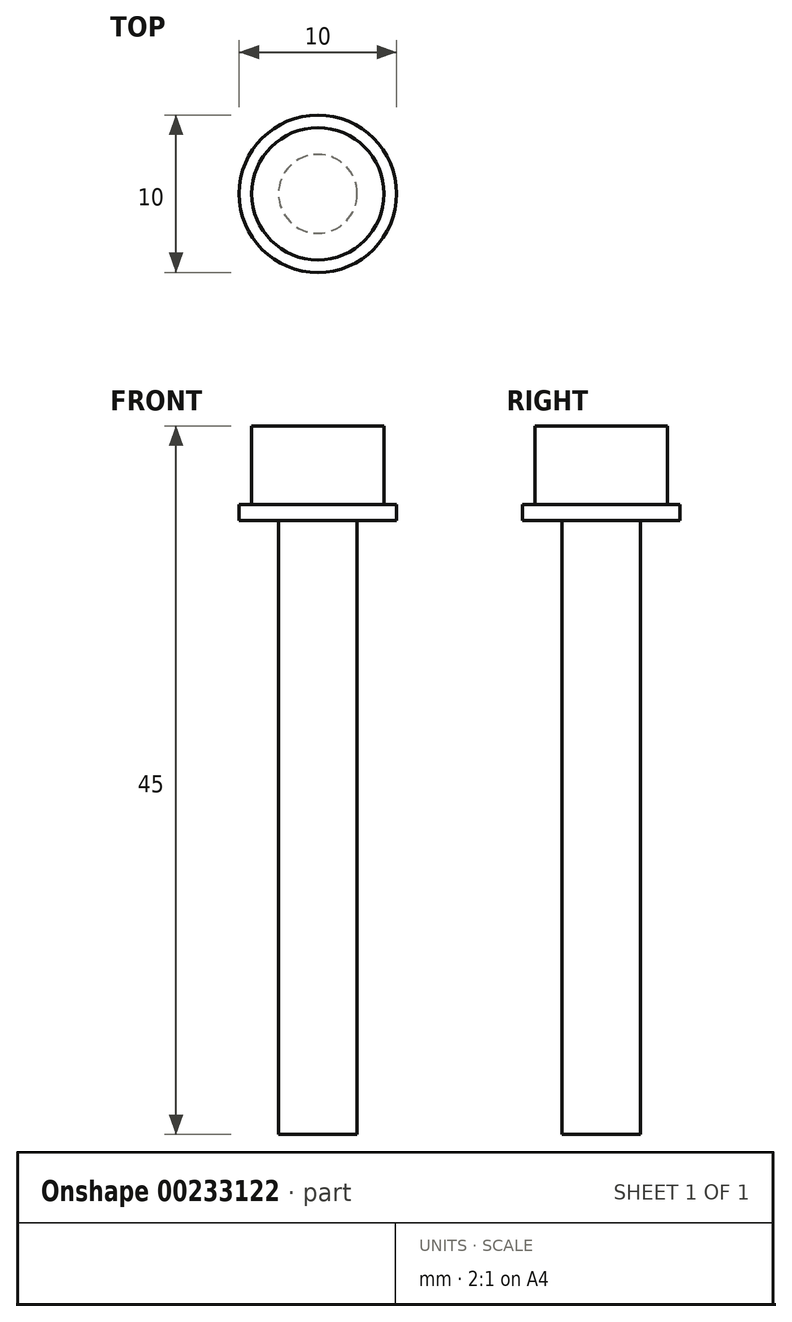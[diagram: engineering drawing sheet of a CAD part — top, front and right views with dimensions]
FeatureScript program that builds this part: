
annotation { "Feature Type Name" : "Feature", "Feature Type Description" : "" }
export const myFeature = defineFeature(function(context is Context, id is Id, definition is map)
    precondition{}
    {
        {
            var Q0;
            Q0=qCreatedBy(makeId("Top.planeOp"),FACE);
            var sketch = newSketch(context, id + "F0", { "sketchPlane" : qUnion([Q0])});
            skCircle(sketch, "E0", {"center": v(0, 0) * mm, "radius": 2.5 * mm});
            skSolve(sketch);
        }
        {
            var Q0;
            Q0 = qSketchRegion(id + "F0", true);
            extrude(context, id + "F1", {"entities" : qUnion([Q0]), "oppositeDirection" : true, "depth" : 40 * mm});
        }
        {
            var Q0;
            Q0=qCreatedBy(makeId("Top.planeOp"),FACE);
            var sketch = newSketch(context, id + "F2", { "sketchPlane" : qUnion([Q0])});
            skCircle(sketch, "E1", {"center": v(0, 0) * mm, "radius": 4.2 * mm});
            skSolve(sketch);
        }
        {
            var Q0;
            Q0 = qSketchRegion(id + "F2", true);
            extrude(context, id + "F3", {"entities" : qUnion([Q0]), "operationType" : NewBodyOperationType.ADD, "depth" : 5 * mm});
        }
        {
            var Q0;
            Q0=qCreatedBy(makeId("Top.planeOp"),FACE);
            var sketch = newSketch(context, id + "F4", { "sketchPlane" : qUnion([Q0])});
            skCircle(sketch, "E2", {"center": v(0, 0) * mm, "radius": 5 * mm});
            skSolve(sketch);
        }
        {
            var Q0;
            Q0 = qSketchRegion(id + "F4", true);
            extrude(context, id + "F5", {"entities" : qUnion([Q0]), "operationType" : NewBodyOperationType.ADD, "oppositeDirection" : true, "depth" : 1 * mm});
        }
    });
